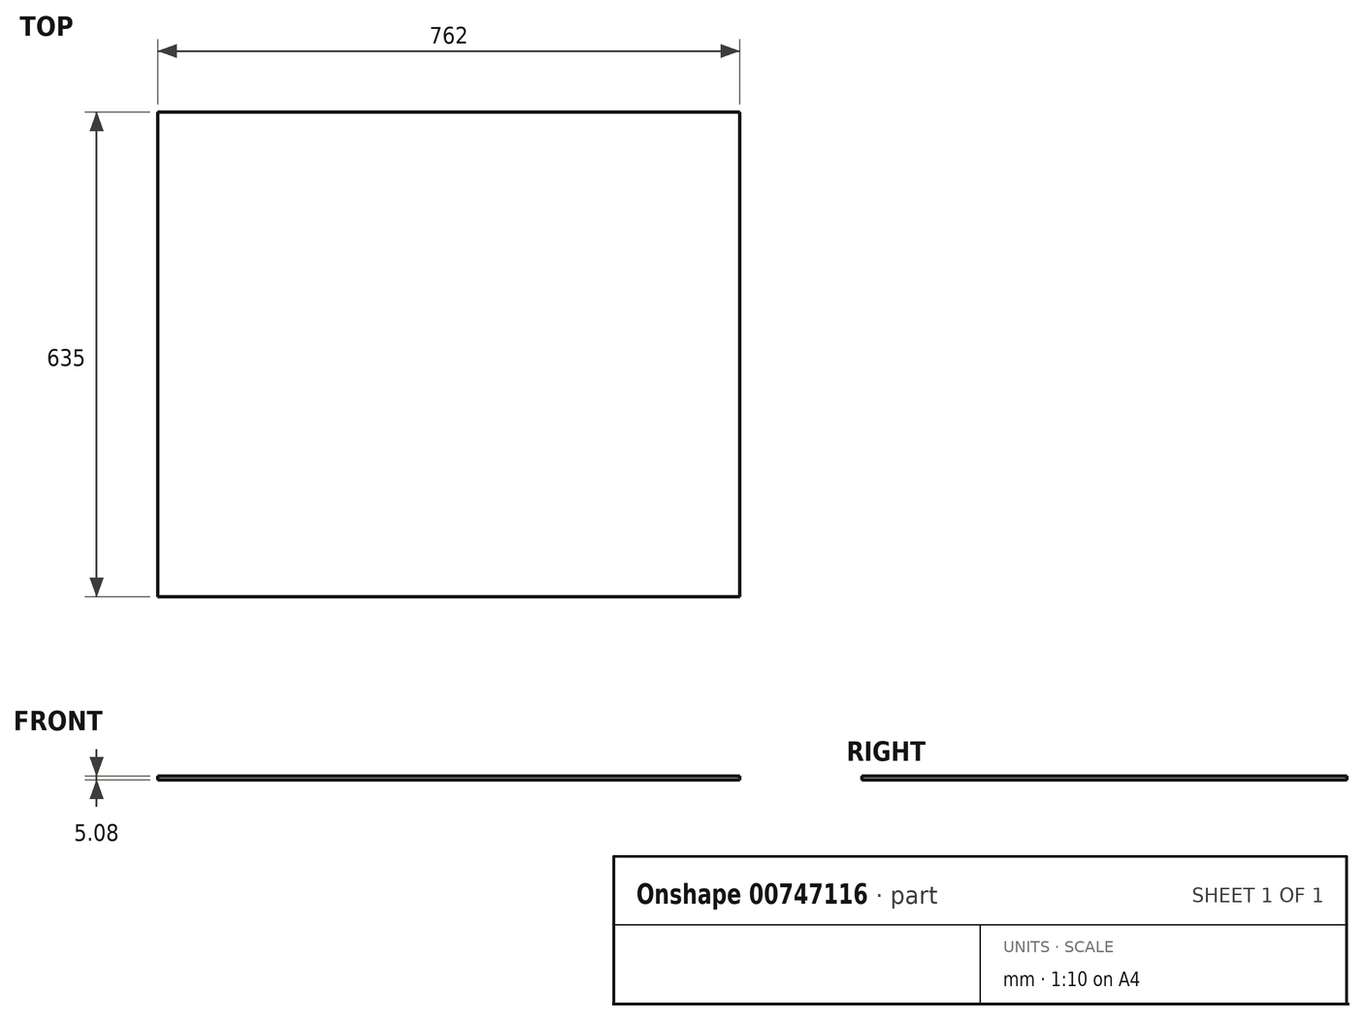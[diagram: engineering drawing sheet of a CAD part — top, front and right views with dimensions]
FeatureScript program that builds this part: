
annotation { "Feature Type Name" : "Feature", "Feature Type Description" : "" }
export const myFeature = defineFeature(function(context is Context, id is Id, definition is map)
    precondition{}
    {
        {
            var Q0;
            Q0=qCreatedBy(makeId("Top.planeOp"),FACE);
            var sketch = newSketch(context, id + "F0", { "sketchPlane" : qUnion([Q0])});
            skLineSegment(sketch, "E0.bottom", {"start": v(381, 317.5) * mm, "end": v(-381, 317.5) * mm});
            skLineSegment(sketch, "E0.top", {"start": v(381, -317.5) * mm, "end": v(-381, -317.5) * mm});
            skLineSegment(sketch, "E0.left", {"start": v(381, 317.5) * mm, "end": v(381, -317.5) * mm});
            skLineSegment(sketch, "E0.right", {"start": v(-381, 317.5) * mm, "end": v(-381, -317.5) * mm});
            skPoint(sketch, "E0.middle", {"position": v(0, 0) * mm});
            skSolve(sketch);
        }
        {
            var Q0;
            Q0=makeQuery(id+"F0.imprint","IMPRINT",FACE,{"disambiguationData":[TD([[makeQuery(id+"F0.imprint","IMPRINT",EDGE,{"derivedFrom":sQuery(id+"F0.wireOp",EDGE,"E0.bottom")}),1.0]])]});
            extrude(context, id + "F1", {"entities" : qUnion([Q0]), "depth" : 5.08 * mm, "offsetDistance" : 25.4 * mm});
        }
    });
